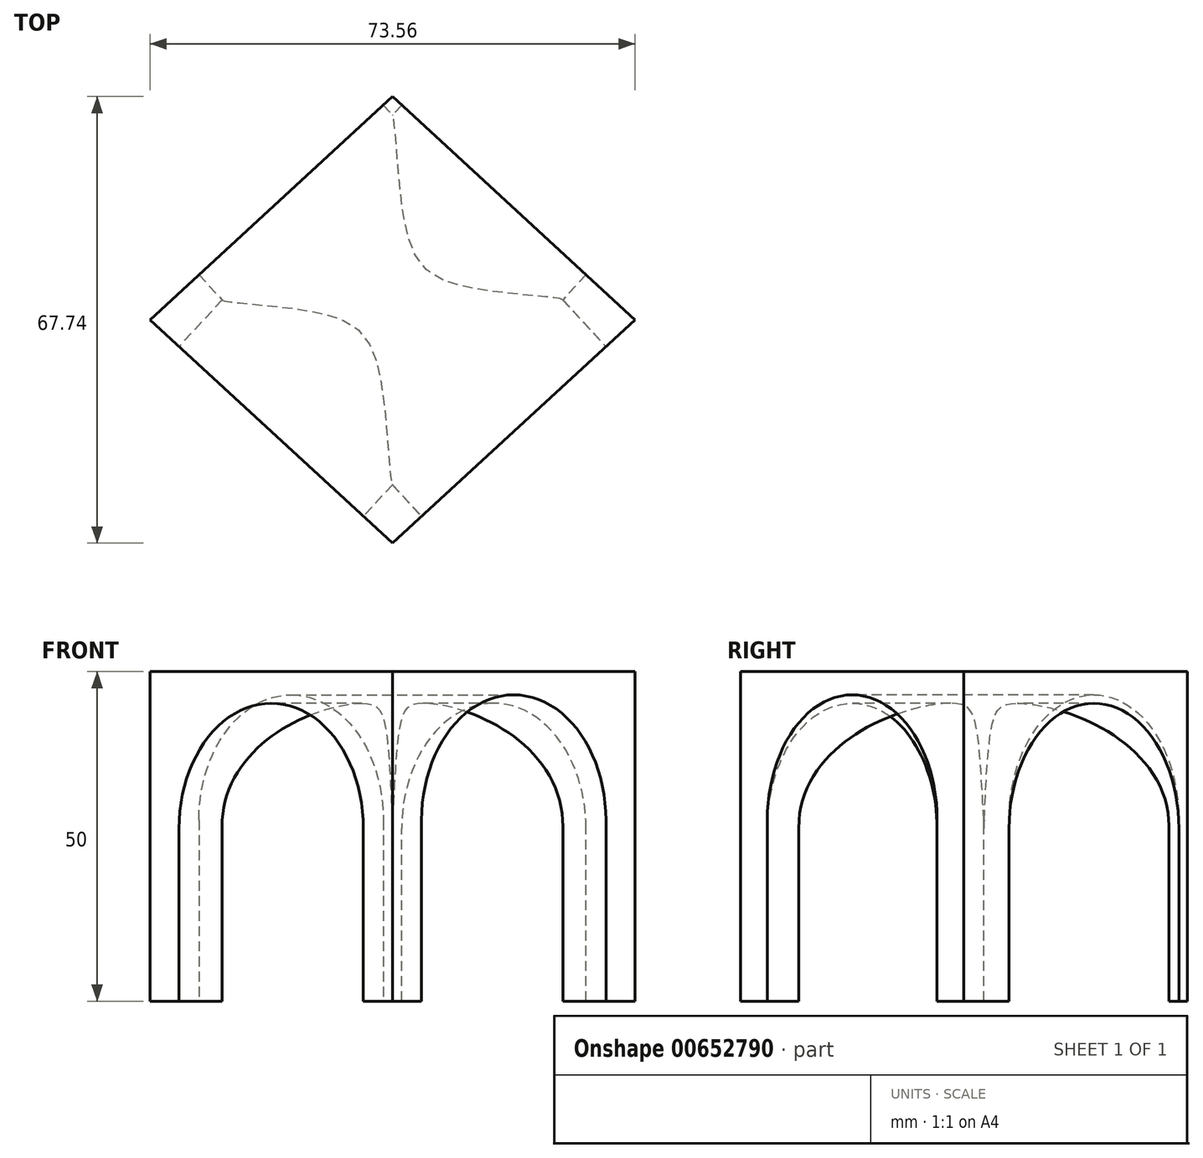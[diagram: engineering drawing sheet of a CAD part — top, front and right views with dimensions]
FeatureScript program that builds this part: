
annotation { "Feature Type Name" : "Feature", "Feature Type Description" : "" }
export const myFeature = defineFeature(function(context is Context, id is Id, definition is map)
    precondition{}
    {
        {
            var Q0;
            Q0=qCreatedBy(makeId("Top.planeOp"),FACE);
            var sketch = newSketch(context, id + "F0", { "sketchPlane" : qUnion([Q0])});
            skLineSegment(sketch, "E0", {"start": v(0, 33.87) * mm, "end": v(-36.78, 0) * mm});
            skLineSegment(sketch, "E1", {"start": v(-36.78, 0) * mm, "end": v(0, -33.87) * mm});
            skLineSegment(sketch, "E2", {"start": v(0, 42.71) * mm, "end": v(0, -35.56) * mm, "construction": true});
            skLineSegment(sketch, "E3.MirrorCS", {"start": v(0, 33.87) * mm, "end": v(36.78, 0) * mm});
            skLineSegment(sketch, "E4.MirrorCS", {"start": v(36.78, 0) * mm, "end": v(0, -33.87) * mm});
            skSolve(sketch);
        }
        {
            var Q0;
            Q0 = qSketchRegion(id + "F0", true);
            extrude(context, id + "F1", {"entities" : qUnion([Q0]), "oppositeDirection" : true, "depth" : 50 * mm, "offsetDistance" : 25 * mm});
        }
        {
            var Q0;
            Q0=makeQuery(id+"F1.opExtrude","SWEPT_FACE",FACE,{"disambiguationData":[OSD([sQuery(id+"F0.wireOp",EDGE,"E1")])]});
            var sketch = newSketch(context, id + "F2", { "sketchPlane" : qUnion([Q0])});
            skLineSegment(sketch, "E5", {"start": v(-21.05, -50) * mm, "end": v(-21.05, -21.9) * mm});
            skPoint(sketch, "E6.startSnap0", {"position": v(-27.05, -25) * mm});
            skArc(sketch, "E7", {"start": v(16.95, -23.8) * mm, "mid": v(-2.05, -4.8) * mm, "end": v(-21.05, -23.8) * mm});
            skLineSegment(sketch, "E8.MirrorCS", {"start": v(16.95, -50) * mm, "end": v(16.95, -21.9) * mm});
            skPoint(sketch, "E9.start.orphan", {"position": v(0, 12.7) * mm});
            skLineSegment(sketch, "E10", {"start": v(-21.05, -50) * mm, "end": v(16.95, -50) * mm});
            skSolve(sketch);
        }
        {
            var Q0;
            {var subQ3=sQuery(id+"F2.wireOp",EDGE,"E7");Q0=makeQuery(id+"F2.imprint","IMPRINT",FACE,{"disambiguationData":[TD([[makeQuery(id+"F2.imprint","IMPRINT",EDGE,{"derivedFrom":subQ3}),1.0]])]});}
            extrude(context, id + "F3", {"entities" : qUnion([Q0]), "operationType" : NewBodyOperationType.REMOVE, "oppositeDirection" : true, "depth" : 50 * mm, "offsetDistance" : 25 * mm});
        }
        {
            var Q0;
            Q0=makeQuery(id+"F1.opExtrude","SWEPT_FACE",FACE,{"disambiguationData":[OSD([sQuery(id+"F0.wireOp",EDGE,"E4.MirrorCS")])]});
            var sketch = newSketch(context, id + "F4", { "sketchPlane" : qUnion([Q0])});
            skLineSegment(sketch, "E11", {"start": v(-16.95, -50) * mm, "end": v(-16.95, -21.5) * mm});
            skLineSegment(sketch, "E12", {"start": v(21.05, -50) * mm, "end": v(21.05, -21.5) * mm});
            skArc(sketch, "E13", {"start": v(21.05, -22.53) * mm, "mid": v(2.05, -3.53) * mm, "end": v(-16.95, -22.53) * mm});
            skPoint(sketch, "E13.centerSnap0", {"position": v(2.05, 0) * mm});
            skSolve(sketch);
        }
        {
            var Q0;
            {var subQ3=sQuery(id+"F4.wireOp",EDGE,"E13");Q0=makeQuery(id+"F4.imprint","IMPRINT",FACE,{"disambiguationData":[TD([[makeQuery(id+"F4.imprint","IMPRINT",EDGE,{"derivedFrom":subQ3}),1.0]])]});}
            extrude(context, id + "F5", {"entities" : qUnion([Q0]), "operationType" : NewBodyOperationType.REMOVE, "endBound" : BoundingType.THROUGH_ALL, "oppositeDirection" : true, "depth" : 25 * mm, "offsetDistance" : 25 * mm});
        }
    });
